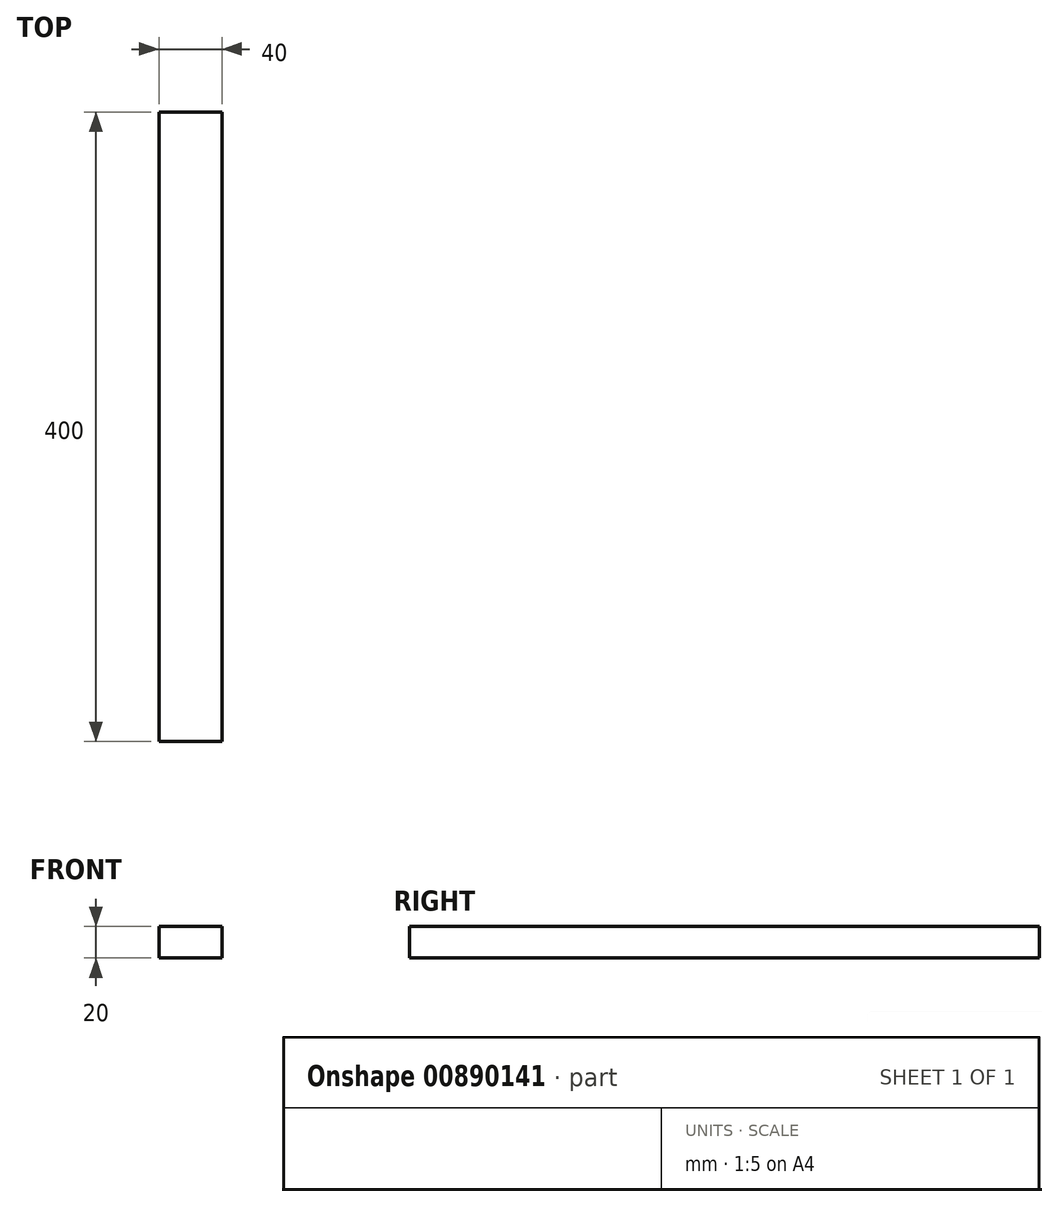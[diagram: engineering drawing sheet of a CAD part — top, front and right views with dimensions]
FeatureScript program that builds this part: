
annotation { "Feature Type Name" : "Feature", "Feature Type Description" : "" }
export const myFeature = defineFeature(function(context is Context, id is Id, definition is map)
    precondition{}
    {
        {
            var Q0;
            Q0=qCreatedBy(makeId("Front.planeOp"),FACE);
            var sketch = newSketch(context, id + "F0", { "sketchPlane" : qUnion([Q0])});
            skLineSegment(sketch, "E0.bottom", {"start": v(-20, 10) * mm, "end": v(20, 10) * mm});
            skLineSegment(sketch, "E0.top", {"start": v(-20, -10) * mm, "end": v(20, -10) * mm});
            skLineSegment(sketch, "E0.left", {"start": v(-20, 10) * mm, "end": v(-20, -10) * mm});
            skLineSegment(sketch, "E0.right", {"start": v(20, 10) * mm, "end": v(20, -10) * mm});
            skPoint(sketch, "E0.middle", {"position": v(0, 0) * mm});
            skSolve(sketch);
        }
        {
            var Q0;
            Q0=qSketchRegion(id+"F0",true);
            extrude(context, id + "F1", {"entities" : qUnion([Q0]), "depth" : 400 * mm, "offsetDistance" : 25 * mm, "symmetric" : true});
        }
    });
